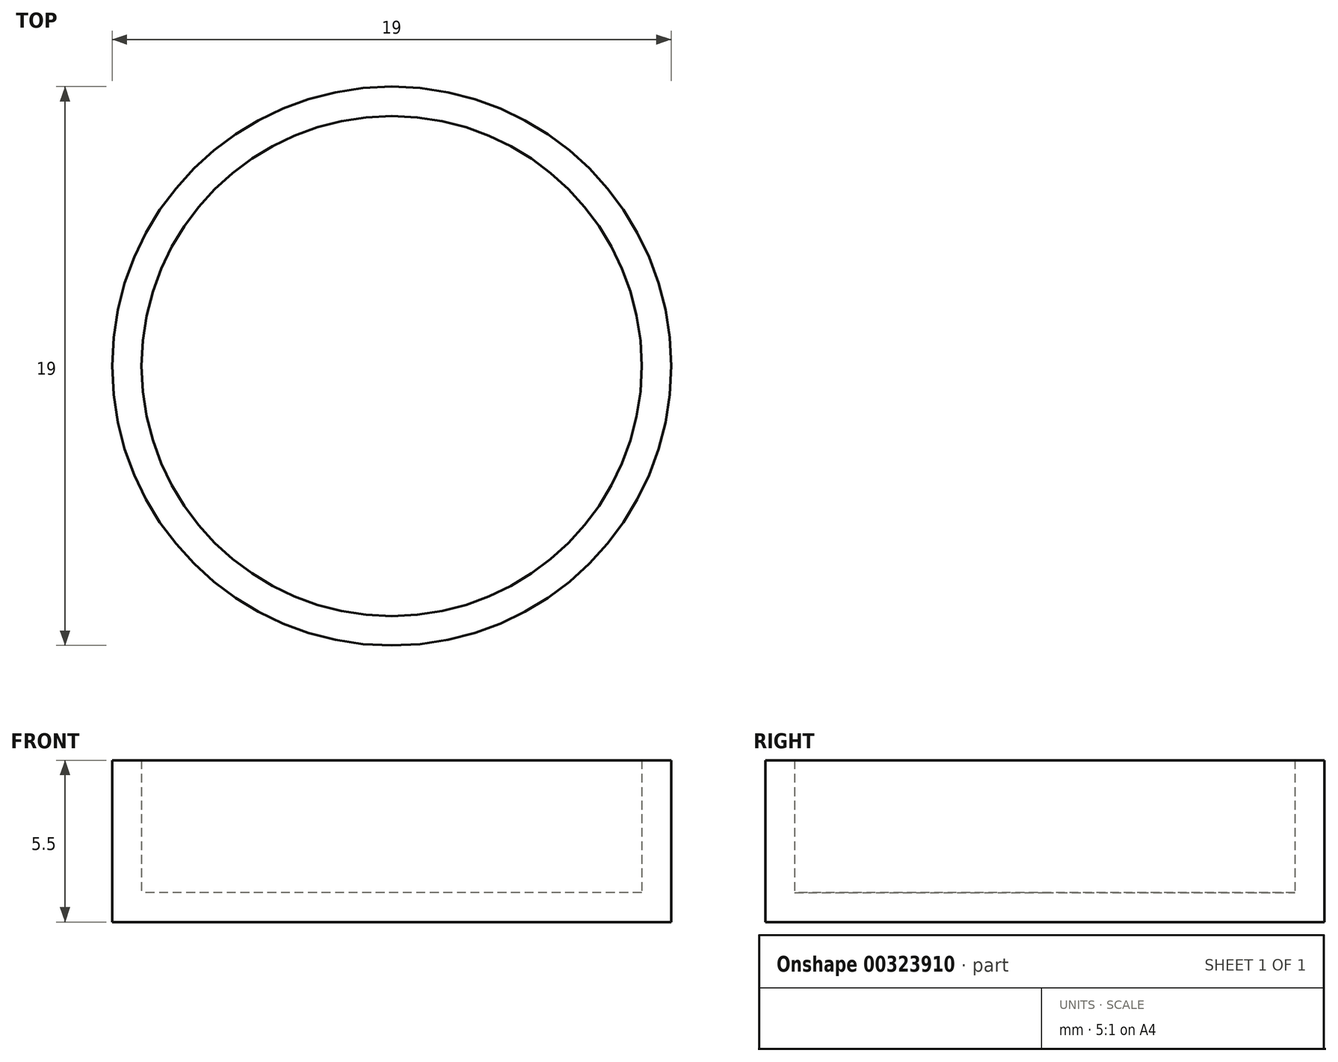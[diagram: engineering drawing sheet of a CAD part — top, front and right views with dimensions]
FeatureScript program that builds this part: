
annotation { "Feature Type Name" : "Feature", "Feature Type Description" : "" }
export const myFeature = defineFeature(function(context is Context, id is Id, definition is map)
    precondition{}
    {
        {
            var Q0;
            Q0=qCreatedBy(makeId("Top.planeOp"),FACE);
            var sketch = newSketch(context, id + "F0", { "sketchPlane" : qUnion([Q0])});
            skCircle(sketch, "E0", {"center": v(0, 0) * mm, "radius": 8.5 * mm});
            skCircle(sketch, "E1", {"center": v(0, 0) * mm, "radius": 9.5 * mm});
            skCircle(sketch, "E2", {"center": v(0, 0) * mm, "radius": 7.5 * mm});
            skCircle(sketch, "E3", {"center": v(0, 0) * mm, "radius": 6.5 * mm});
            skSolve(sketch);
        }
        {
            var Q0;
            Q0=makeQuery(id+"F0.imprint","IMPRINT",FACE,{"disambiguationData":[TD([[makeQuery(id+"F0.imprint","IMPRINT",EDGE,{"derivedFrom":sQuery(id+"F0.wireOp",EDGE,"E0")}),-1.0]])]});
            extrude(context, id + "F1", {"entities" : qUnion([Q0]), "depth" : 4.5 * mm});
        }
        {
            var Q0;
            Q0=makeQuery(id+"F0.imprint","IMPRINT",FACE,{"disambiguationData":[TD([[makeQuery(id+"F0.imprint","IMPRINT",EDGE,{"derivedFrom":sQuery(id+"F0.wireOp",EDGE,"E0")}),-1.0]])]});
            var Q1;
            Q1=makeQuery(id+"F0.imprint","IMPRINT",FACE,{"disambiguationData":[TD([[makeQuery(id+"F0.imprint","IMPRINT",EDGE,{"derivedFrom":sQuery(id+"F0.wireOp",EDGE,"E2")}),1.0]])]});
            var Q2;
            Q2=makeQuery(id+"F0.imprint","IMPRINT",FACE,{"disambiguationData":[TD([[makeQuery(id+"F0.imprint","IMPRINT",EDGE,{"derivedFrom":sQuery(id+"F0.wireOp",EDGE,"E0")}),1.0]])]});
            var Q3;
            Q3=makeQuery(id+"F0.imprint","IMPRINT",FACE,{"disambiguationData":[TD([[makeQuery(id+"F0.imprint","IMPRINT",EDGE,{"derivedFrom":sQuery(id+"F0.wireOp",EDGE,"E3")}),1.0]])]});
            extrude(context, id + "F2", {"entities" : qUnion([Q0, Q1, Q2, Q3]), "operationType" : NewBodyOperationType.ADD, "oppositeDirection" : true, "depth" : 1 * mm});
        }
    });
